# Revit family: 756-106-782-DN150-1200
name_source: partatom
category: Pipe Accessories
units: mm (PartAtom-declared; Revit-internal decimal feet)

## family parameters
Always vertical = Yes
Cut with Voids When Loaded = No
Part Type = Valve - Breaks Into
Round Connector Dimension = Use Diameter
Shared = No
Work Plane-Based = No

## types (14) — shared parameters
Body_wallthickness = 10 mm  [stored 0.0328084 ft]
D1 = 12 mm  [stored 0.0393701 ft]
DN0150 = No
DN0200 = No
DN0250 = No
DN0300 = No
DN0350 = No
DN0400 = No
DN0450 = No
DN0500 = No
DN0600 = No
DN0800 = No
DN0900 = No
DN1000 = No
DN1000_PN25 = 756-1000-1-7400609
DN1200 = No
DN1200_PN25 = 756-1200-1-7400609
DN150_PN25 = 756-0150-1-7400609
DN200_PN25 = 756-0200-1-7400609
DN250_PN25 = 756-0250-1-7400609
DN300_PN25 = 756-0300-1-7400609
DN350_PN25 = 756-0350-1-7400609
DN400_PN25 = 756-0400-1-7400609
DN450_PN25 = 756-0450-1-7400609
DN500_PN25 = 756-0500-1-7400609
DN600_PN25 = 756-0600-1-7400609
DN700_PN25 = 756-0700-1-7400609
DN800_PN25 = 756-0800-1-7400609
DN900_PN25 = 756-0900-1-7400609
Description_ = AVK DOUBLE ECC. BUTTERFLY VALVE, LONG
HW_rod_Dia = 20 mm  [stored 0.0656168 ft]
Pin_dia = 40 mm  [stored 0.131234 ft]
RF_Cut_Thickness = 5 mm  [stored 0.0164042 ft]
Rib_depth = 15 mm  [stored 0.0492126 ft]
Search_table = 756-106-782-DN150-1200
URL_product_pages = https://www.avkvalves.com

## per-type parameters (varying)
- DN0150: Bottom_Depth=225 mm; Bottom_width=120 mm; C_rod=9 mm  [stored 0.0295276 ft]; D=115 mm; DN=150 mm; DN0700=No; Disc _width=10 mm  [stored 0.0328084 ft]; Disc_Dia=133 mm; Flange_OD=143 mm; Flange_Thickness=15 mm  [stored 0.0492126 ft]; Gear_box_Mount_Flange_thickness=15 mm  [stored 0.0492126 ft]; Gear_box_Mount_Flange_width=68 mm  [stored 0.223097 ft]; Gear_box_Mount_width=43 mm  [stored 0.141076 ft]; Gear_box_width=90 mm; H1=191 mm; H2=192 mm; HW_Connecting_Rib=230 mm; HW_Connecting_Rib_ref=225 mm; HW_Ref=71 mm  [stored 0.23294 ft]; HW_height=166 mm; Hand_wheel_rod=37 mm  [stored 0.121391 ft]; ID (Radius)=75 mm; L=210 mm; L1=1 mm  [stored 0.00328084 ft]; L2=1 mm  [stored 0.00328084 ft]; Offset=3 mm  [stored 0.00984252 ft]; Pin_Depth=218 mm; Pin_width=105 mm; Rf_Dia=106 mm; Rib_height=130 mm; Rib_height_2=48 mm  [stored 0.15748 ft]; Rib_width=180 mm; Rib_width_2=136 mm; W1=162 mm; W2=260 mm; W3=6 mm  [stored 0.019685 ft]; W4=6 mm  [stored 0.019685 ft]; W5=176 mm; W5(Addon)=135 mm
- DN0200: Bottom_Depth=300 mm; Bottom_width=140 mm; C_rod=9 mm  [stored 0.0295276 ft]; D=115 mm; DN=200 mm; DN0700=No; Disc _width=10 mm  [stored 0.0328084 ft]; Disc_Dia=180 mm; Flange_OD=170 mm; Flange_Thickness=15 mm  [stored 0.0492126 ft]; Gear_box_Mount_Flange_thickness=15 mm  [stored 0.0492126 ft]; Gear_box_Mount_Flange_width=68 mm  [stored 0.223097 ft]; Gear_box_Mount_width=43 mm  [stored 0.141076 ft]; Gear_box_width=90 mm; H1=217 mm; H2=223 mm; HW_Connecting_Rib=230 mm; HW_Connecting_Rib_ref=252 mm; HW_Ref=71 mm  [stored 0.23294 ft]; HW_height=166 mm; Hand_wheel_rod=32 mm  [stored 0.104987 ft]; ID (Radius)=100 mm; L=230 mm; L1=1 mm  [stored 0.00328084 ft]; L2=1 mm  [stored 0.00328084 ft]; Offset=5 mm  [stored 0.0164042 ft]; Pin_Depth=270 mm; Pin_width=115 mm; Rf_Dia=133 mm; Rib_height=155 mm; Rib_height_2=47 mm; Rib_width=200 mm; Rib_width_2=136 mm; W1=190 mm; W2=288 mm; W3=6 mm  [stored 0.019685 ft]; W4=6 mm  [stored 0.019685 ft]; W5=176 mm; W5(Addon)=135 mm
- DN0250: Bottom_Depth=375 mm; Bottom_width=170 mm; C_rod=14 mm  [stored 0.0459318 ft]; D=115 mm; DN=250 mm; DN0700=No; Disc _width=15 mm  [stored 0.0492126 ft]; Disc_Dia=227 mm; Flange_OD=203 mm; Flange_Thickness=15 mm  [stored 0.0492126 ft]; Gear_box_Mount_Flange_thickness=15 mm  [stored 0.0492126 ft]; Gear_box_Mount_Flange_width=62 mm  [stored 0.203412 ft]; Gear_box_Mount_width=37 mm  [stored 0.121391 ft]; Gear_box_width=82 mm; H1=251 mm; H2=268 mm; HW_Connecting_Rib=230 mm; HW_Connecting_Rib_ref=292 mm; HW_Ref=71 mm  [stored 0.23294 ft]; HW_height=176 mm; Hand_wheel_rod=32 mm  [stored 0.104987 ft]; ID (Radius)=125 mm; L=250 mm; L1=1 mm  [stored 0.00328084 ft]; L2=1 mm  [stored 0.00328084 ft]; Offset=5 mm  [stored 0.0164042 ft]; Pin_Depth=328 mm; Pin_width=125 mm; Rf_Dia=160 mm; Rib_height=184 mm; Rib_height_2=48 mm  [stored 0.15748 ft]; Rib_width=220 mm; Rib_width_2=124 mm; W1=223 mm; W2=333 mm; W3=6 mm  [stored 0.019685 ft]; W4=6 mm  [stored 0.019685 ft]; W5=186 mm; W5(Addon)=143 mm
- DN0300: Bottom_Depth=450 mm; Bottom_width=210 mm; C_rod=14 mm  [stored 0.0459318 ft]; D=190 mm; DN=300 mm; DN0700=No; Disc _width=15 mm  [stored 0.0492126 ft]; Disc_Dia=282 mm; Flange_OD=230 mm; Flange_Thickness=20 mm  [stored 0.0656168 ft]; Gear_box_Mount_Flange_thickness=20 mm  [stored 0.0656168 ft]; Gear_box_Mount_Flange_width=75 mm; Gear_box_Mount_width=45 mm  [stored 0.147638 ft]; Gear_box_width=99 mm; H1=282 mm; H2=303 mm; HW_Connecting_Rib=380 mm; HW_Connecting_Rib_ref=325 mm; HW_Ref=71 mm  [stored 0.23294 ft]; HW_height=176 mm; Hand_wheel_rod=31 mm  [stored 0.101706 ft]; ID (Radius)=150 mm; L=270 mm; L1=1 mm  [stored 0.00328084 ft]; L2=12 mm  [stored 0.0393701 ft]; Offset=6 mm  [stored 0.019685 ft]; Pin_Depth=380 mm; Pin_width=135 mm; Rf_Dia=185 mm; Rib_height=209 mm; Rib_height_2=52 mm; Rib_width=230 mm; Rib_width_2=150 mm; W1=253 mm; W2=368 mm; W3=17 mm  [stored 0.0557743 ft]; W4=115 mm; W5=186 mm; W5(Addon)=143 mm
- DN0350: Bottom_Depth=525 mm; Bottom_width=210 mm; C_rod=19 mm  [stored 0.062336 ft]; D=190 mm; DN=350 mm; DN0700=No; Disc _width=20 mm  [stored 0.0656168 ft]; Disc_Dia=334 mm; Flange_OD=260 mm; Flange_Thickness=20 mm  [stored 0.0656168 ft]; Gear_box_Mount_Flange_thickness=20 mm  [stored 0.0656168 ft]; Gear_box_Mount_Flange_width=80 mm; Gear_box_Mount_width=50 mm  [stored 0.164042 ft]; Gear_box_width=106 mm; H1=308 mm; H2=331 mm; HW_Connecting_Rib=380 mm; HW_Connecting_Rib_ref=351 mm; HW_Ref=71 mm  [stored 0.23294 ft]; HW_height=176 mm; Hand_wheel_rod=31 mm  [stored 0.101706 ft]; ID (Radius)=175 mm; L=290 mm; L1=19 mm  [stored 0.062336 ft]; L2=25 mm  [stored 0.082021 ft]; Offset=3 mm  [stored 0.00984252 ft]; Pin_Depth=435 mm; Pin_width=145 mm; Rf_Dia=215 mm; Rib_height=236 mm; Rib_height_2=48 mm  [stored 0.15748 ft]; Rib_width=250 mm; Rib_width_2=160 mm; W1=288 mm; W2=393 mm; W3=155 mm; W4=176 mm; W5=186 mm; W5(Addon)=143 mm
- DN0400: Bottom_Depth=600 mm; Bottom_width=260 mm; C_rod=24 mm  [stored 0.0787402 ft]; D=190 mm; DN=400 mm; DN0700=No; Disc _width=25 mm  [stored 0.082021 ft]; Disc_Dia=383 mm; Flange_OD=290 mm; Flange_Thickness=20 mm  [stored 0.0656168 ft]; Gear_box_Mount_Flange_thickness=20 mm  [stored 0.0656168 ft]; Gear_box_Mount_Flange_width=75 mm; Gear_box_Mount_width=45 mm  [stored 0.147638 ft]; Gear_box_width=99 mm; H1=350 mm; H2=373 mm; HW_Connecting_Rib=380 mm; HW_Connecting_Rib_ref=393 mm; HW_Ref=80 mm; HW_height=176 mm; Hand_wheel_rod=32 mm  [stored 0.104987 ft]; ID (Radius)=200 mm; L=310 mm; L1=34 mm  [stored 0.111549 ft]; L2=40 mm  [stored 0.131234 ft]; Offset=3 mm  [stored 0.00984252 ft]; Pin_Depth=490 mm; Pin_width=155 mm; Rf_Dia=240 mm; Rib_height=264 mm; Rib_height_2=60 mm; Rib_width=270 mm; Rib_width_2=150 mm; W1=320 mm; W2=435 mm; W3=217 mm; W4=234 mm; W5=186 mm; W5(Addon)=143 mm
- DN0450: Bottom_Depth=675 mm; Bottom_width=280 mm; C_rod=24 mm  [stored 0.0787402 ft]; D=240 mm; DN=450 mm; DN0700=No; Disc _width=25 mm  [stored 0.082021 ft]; Disc_Dia=432 mm; Flange_OD=320 mm; Flange_Thickness=30 mm  [stored 0.0984252 ft]; Gear_box_Mount_Flange_thickness=30 mm  [stored 0.0984252 ft]; Gear_box_Mount_Flange_width=93 mm; Gear_box_Mount_width=58 mm  [stored 0.190289 ft]; Gear_box_width=122 mm; H1=390 mm; H2=411 mm; HW_Connecting_Rib=480 mm; HW_Connecting_Rib_ref=447 mm; HW_Ref=86 mm; HW_height=252 mm; Hand_wheel_rod=30 mm  [stored 0.0984252 ft]; ID (Radius)=225 mm; L=330 mm; L1=48 mm  [stored 0.15748 ft]; L2=54 mm  [stored 0.177165 ft]; Offset=3 mm  [stored 0.00984252 ft]; Pin_Depth=545 mm; Pin_width=165 mm; Rf_Dia=265 mm; Rib_height=291 mm; Rib_height_2=70 mm; Rib_width=270 mm; Rib_width_2=185 mm; W1=345 mm; W2=503 mm; W3=270 mm; W4=285 mm; W5=262 mm; W5(Addon)=202 mm
- DN0500: Bottom_Depth=750 mm; Bottom_width=320 mm; C_rod=34 mm  [stored 0.111549 ft]; D=240 mm; DN=500 mm; DN0700=No; Disc _width=35 mm  [stored 0.114829 ft]; Disc_Dia=483 mm; Flange_OD=335 mm; Flange_Thickness=30 mm  [stored 0.0984252 ft]; Gear_box_Mount_Flange_thickness=30 mm  [stored 0.0984252 ft]; Gear_box_Mount_Flange_width=93 mm; Gear_box_Mount_width=58 mm  [stored 0.190289 ft]; Gear_box_width=122 mm; H1=425 mm; H2=454 mm; HW_Connecting_Rib=480 mm; HW_Connecting_Rib_ref=486 mm; HW_Ref=86 mm; HW_height=252 mm; Hand_wheel_rod=30 mm  [stored 0.0984252 ft]; ID (Radius)=250 mm; L=350 mm; L1=63 mm  [stored 0.206693 ft]; L2=69 mm  [stored 0.226378 ft]; Offset=3 mm  [stored 0.00984252 ft]; Pin_Depth=585 mm; Pin_width=175 mm; Rf_Dia=291 mm; Rib_height=305 mm; Rib_height_2=90 mm; Rib_width=290 mm; Rib_width_2=185 mm; W1=375 mm; W2=546 mm; W3=325 mm; W4=338 mm; W5=262 mm; W5(Addon)=202 mm
- DN0600: Bottom_Depth=900 mm; Bottom_width=400 mm; C_rod=34 mm  [stored 0.111549 ft]; D=290 mm; DN=600 mm; DN0700=No; Disc _width=35 mm  [stored 0.114829 ft]; Disc_Dia=580 mm; Flange_OD=390 mm; Flange_Thickness=30 mm  [stored 0.0984252 ft]; Gear_box_Mount_Flange_thickness=30 mm  [stored 0.0984252 ft]; Gear_box_Mount_Flange_width=103 mm; Gear_box_Mount_width=63 mm  [stored 0.206693 ft]; Gear_box_width=135 mm; H1=510 mm; H2=541 mm; HW_Connecting_Rib=580 mm; HW_Connecting_Rib_ref=571 mm; HW_Ref=104 mm; HW_height=329 mm; Hand_wheel_rod=32 mm  [stored 0.104987 ft]; ID (Radius)=300 mm; L=390 mm; L1=92 mm; L2=98 mm; Offset=3 mm  [stored 0.00984252 ft]; Pin_Depth=690 mm; Pin_width=195 mm; Rf_Dia=341 mm; Rib_height=355 mm; Rib_height_2=120 mm; Rib_width=330 mm; Rib_width_2=205 mm; W1=430 mm; W2=632 mm; W3=424 mm; W4=434 mm; W5=339 mm; W5(Addon)=261 mm
- DN0700: Bottom_Depth=1050 mm; Bottom_width=427 mm; C_rod=34 mm  [stored 0.111549 ft]; D=340 mm; DN=700 mm; DN0700=Yes; Disc _width=35 mm  [stored 0.114829 ft]; Disc_Dia=684 mm; Flange_OD=455 mm; Flange_Thickness=40 mm  [stored 0.131234 ft]; Gear_box_Mount_Flange_thickness=30 mm  [stored 0.0984252 ft]; Gear_box_Mount_Flange_width=102 mm; Gear_box_Mount_width=62 mm  [stored 0.203412 ft]; Gear_box_width=135 mm; H1=535 mm; H2=566 mm; HW_Connecting_Rib=680 mm; HW_Connecting_Rib_ref=621 mm; HW_Ref=110 mm; HW_height=381 mm; Hand_wheel_rod=33 mm  [stored 0.108268 ft]; ID (Radius)=350 mm; L=430 mm; L1=124 mm; L2=130 mm; Offset=3 mm  [stored 0.00984252 ft]; Pin_Depth=805 mm; Pin_width=215 mm; Rf_Dia=397 mm; Rib_height=414 mm; Rib_height_2=80 mm; Rib_width=350 mm; Rib_width_2=204 mm; W1=483 mm; W2=706 mm; W3=527 mm; W4=537 mm; W5=391 mm; W5(Addon)=301 mm
- DN0800: Bottom_Depth=1200 mm; Bottom_width=460 mm; C_rod=34 mm  [stored 0.111549 ft]; D=340 mm; DN=800 mm; DN0700=Yes; Disc _width=35 mm  [stored 0.114829 ft]; Disc_Dia=787 mm; Flange_OD=513 mm; Flange_Thickness=40 mm  [stored 0.131234 ft]; Gear_box_Mount_Flange_thickness=40 mm  [stored 0.131234 ft]; Gear_box_Mount_Flange_width=112 mm; Gear_box_Mount_width=68 mm  [stored 0.223097 ft]; Gear_box_width=147 mm; H1=620 mm; H2=650 mm; HW_Connecting_Rib=680 mm; HW_Connecting_Rib_ref=718 mm; HW_Ref=125 mm; HW_height=381 mm; Hand_wheel_rod=36 mm  [stored 0.11811 ft]; ID (Radius)=400 mm; L=470 mm; L1=155 mm; L2=161 mm; Offset=3 mm  [stored 0.00984252 ft]; Pin_Depth=913 mm; Pin_width=235 mm; Rf_Dia=450 mm; Rib_height=466 mm; Rib_height_2=108 mm; Rib_width=390 mm; Rib_width_2=223 mm; W1=546 mm; W2=815 mm; W3=626 mm; W4=635 mm; W5=391 mm; W5(Addon)=301 mm
- DN0900: Bottom_Depth=1350 mm; Bottom_width=524 mm; C_rod=34 mm  [stored 0.111549 ft]; D=340 mm; DN=900 mm; DN0700=Yes; Disc _width=35 mm  [stored 0.114829 ft]; Disc_Dia=887 mm; Flange_OD=562 mm; Flange_Thickness=40 mm  [stored 0.131234 ft]; Gear_box_Mount_Flange_thickness=40 mm  [stored 0.131234 ft]; Gear_box_Mount_Flange_width=121 mm; Gear_box_Mount_width=74 mm; Gear_box_width=159 mm; H1=674 mm; H2=701 mm; HW_Connecting_Rib=680 mm; HW_Connecting_Rib_ref=770 mm; HW_Ref=128 mm; HW_height=381 mm; Hand_wheel_rod=39 mm  [stored 0.127953 ft]; ID (Radius)=450 mm; L=510 mm; L1=185 mm; L2=191 mm; Offset=3 mm  [stored 0.00984252 ft]; Pin_Depth=1012 mm; Pin_width=255 mm; Rf_Dia=500 mm; Rib_height=511 mm; Rib_height_2=112 mm; Rib_width=430 mm; Rib_width_2=241 mm; W1=593 mm; W2=865 mm; W3=721 mm; W4=729 mm; W5=391 mm; W5(Addon)=301 mm
- DN1000: Bottom_Depth=1500 mm; Bottom_width=588 mm; C_rod=34 mm  [stored 0.111549 ft]; D=340 mm; DN=1000 mm; DN0700=Yes; Disc _width=35 mm  [stored 0.114829 ft]; Disc_Dia=988 mm; Flange_OD=628 mm; Flange_Thickness=40 mm  [stored 0.131234 ft]; Gear_box_Mount_Flange_thickness=40 mm  [stored 0.131234 ft]; Gear_box_Mount_Flange_width=130 mm; Gear_box_Mount_width=80 mm; Gear_box_width=171 mm; H1=745 mm; H2=771 mm; HW_Connecting_Rib=680 mm; HW_Connecting_Rib_ref=840 mm; HW_Ref=130 mm; HW_height=381 mm; Hand_wheel_rod=42 mm  [stored 0.137795 ft]; ID (Radius)=500 mm; L=550 mm; L1=216 mm; L2=222 mm; Offset=3 mm  [stored 0.00984252 ft]; Pin_Depth=1128 mm; Pin_width=275 mm; Rf_Dia=556 mm; Rib_height=570 mm; Rib_height_2=118 mm; Rib_width=470 mm; Rib_width_2=259 mm; W1=663 mm; W2=935 mm; W3=813 mm; W4=824 mm; W5=391 mm; W5(Addon)=301 mm
- DN1200: Bottom_Depth=1800 mm; Bottom_width=653 mm; C_rod=34 mm  [stored 0.111549 ft]; D=340 mm; DN=1200 mm; DN0700=Yes; Disc _width=35 mm  [stored 0.114829 ft]; Disc_Dia=1173 mm; Flange_OD=743 mm; Flange_Thickness=40 mm  [stored 0.131234 ft]; Gear_box_Mount_Flange_thickness=40 mm  [stored 0.131234 ft]; Gear_box_Mount_Flange_width=139 mm; Gear_box_Mount_width=84 mm; Gear_box_width=183 mm; H1=850 mm; H2=899 mm; HW_Connecting_Rib=680 mm; HW_Connecting_Rib_ref=941 mm; HW_Ref=128 mm; HW_height=442 mm; Hand_wheel_rod=45 mm  [stored 0.147638 ft]; ID (Radius)=600 mm; L=630 mm; L1=268 mm; L2=272 mm; Offset=3 mm  [stored 0.00984252 ft]; Pin_Depth=1343 mm; Pin_width=315 mm; Rf_Dia=666 mm; Rib_height=675 mm; Rib_height_2=108 mm; Rib_width=550 mm; Rib_width_2=277 mm; W1=768 mm; W2=1031 mm; W3=982 mm; W4=987 mm; W5=452 mm; W5(Addon)=348 mm

note: [stored X ft] marks values corroborated as IEEE doubles in the binary element streams (Revit-internal decimal feet)

## geometry (parser evidence)
native form markers: Sweep x7
no freeform markers — native parametric forms only
